# Revit family: 3D-AKE-00063268
name_source: partatom
category: Allgemeines Modell
units: mm (PartAtom-declared; Revit-internal decimal feet)

## family parameters
Arbeitsebenenbasiert = Nein
Beim Laden mit Abzugskörper schneiden = Nein
Bemaßung runder Anschluss = Durchmesser verwenden
Beschriftungsausrichtung beibehalten = Nein
Gemeinsam genutzt = Nein
Immer vertikal = Ja
Kann Basisbauteil für Bewehrung sein = Nein
Raumberechnungspunkt = Nein
Teiletyp = Normal

## types (1)
- Norm
    Abwicklungshöhe = 0
    Abwicklungslänge = 0
    Artikelvorlage = 00900016
    Bauteilnummer = 3D-AKE-00063268
    Breite = 1200
    DocNumber = 3D-AKE-00062680
    Entstanden aus = 3D-AKE-00063258.ipt
    Ersatzteilkennung = nein
    Erstellungsdatum = 23.10.2024
    Folder = <userpath>\.\
    Gewicht = 3247,35 kg
    Höhe = 1610
    Kennung = Standardteil
    Konstruktionsstatus = 1
    Revisionsnummer = -
    Tiefe = 674,5
    Titel = Green Caleo Cold 120-161 RAL9005
    VDS_Category = 3D-Konstruktion Bauteil
    Vorgabe-Ansicht = 0 mm  [stored 0 ft]

note: [stored X ft] marks values corroborated as IEEE doubles in the binary element streams (Revit-internal decimal feet)
